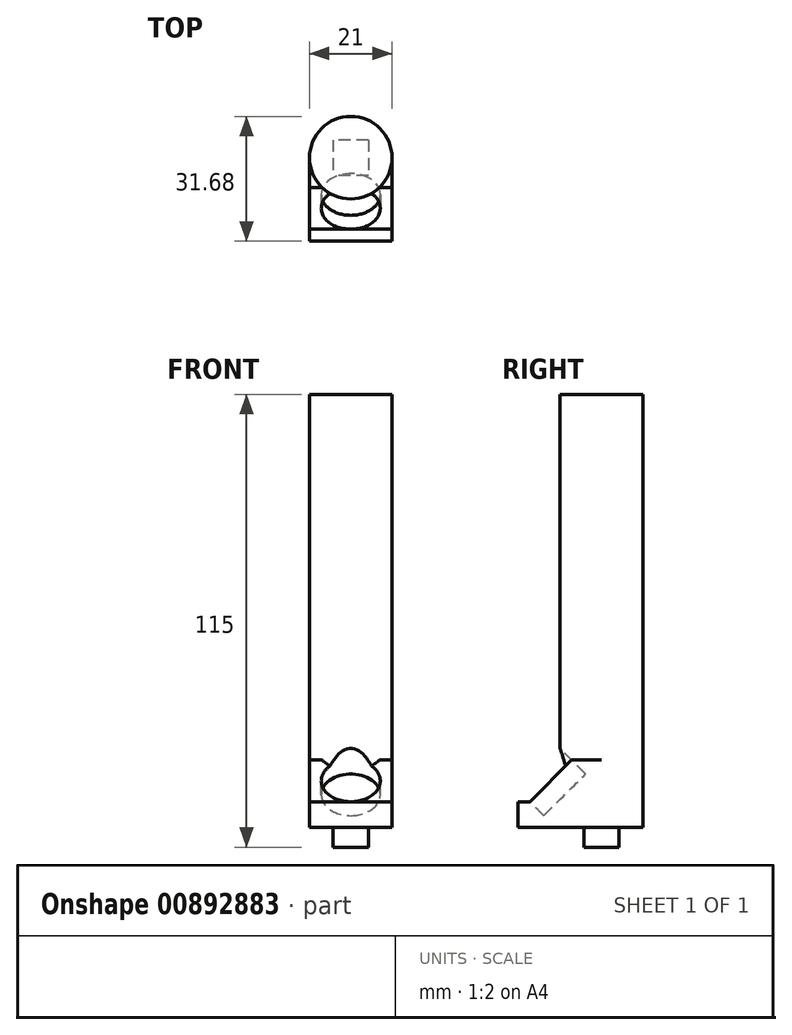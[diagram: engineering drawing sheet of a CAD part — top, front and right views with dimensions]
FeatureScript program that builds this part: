
annotation { "Feature Type Name" : "Feature", "Feature Type Description" : "" }
export const myFeature = defineFeature(function(context is Context, id is Id, definition is map)
    precondition{}
    {
        {
            var Q0;
            Q0=qCreatedBy(makeId("Top.planeOp"),FACE);
            var sketch = newSketch(context, id + "F0", { "sketchPlane" : qUnion([Q0])});
            skCircle(sketch, "E0", {"center": v(0, 0) * mm, "radius": 10.5 * mm});
            skSolve(sketch);
        }
        {
            var Q0;
            Q0=makeQuery(id+"F0.imprint","IMPRINT",FACE,{"disambiguationData":[TD([[makeQuery(id+"F0.imprint","IMPRINT",EDGE,{"derivedFrom":sQuery(id+"F0.wireOp",EDGE,"E0")}),1.0]])]});
            var Q1;
            Q1=sQuery(id+"F0.wireOp",EDGE,"E0");
            extrude(context, id + "F1", {"entities" : qUnion([Q0]), "surfaceEntities" : qUnion([Q1]), "depth" : 110 * mm, "offsetDistance" : 25 * mm});
        }
        {
            var Q0;
            Q0=qCreatedBy(makeId("Top.planeOp"),FACE);
            var sketch = newSketch(context, id + "F2", { "sketchPlane" : qUnion([Q0])});
            skLineSegment(sketch, "E1.bottom", {"start": v(4.5, 4.5) * mm, "end": v(-4.5, 4.5) * mm});
            skLineSegment(sketch, "E1.top", {"start": v(4.5, -4.5) * mm, "end": v(-4.5, -4.5) * mm});
            skLineSegment(sketch, "E1.left", {"start": v(4.5, 4.5) * mm, "end": v(4.5, -4.5) * mm});
            skLineSegment(sketch, "E1.right", {"start": v(-4.5, 4.5) * mm, "end": v(-4.5, -4.5) * mm});
            skPoint(sketch, "E1.middle", {"position": v(0, 0) * mm});
            skSolve(sketch);
        }
        {
            var Q0;
            Q0 = qSketchRegion(id + "F2", true);
            extrude(context, id + "F3", {"entities" : qUnion([Q0]), "operationType" : NewBodyOperationType.ADD, "oppositeDirection" : true, "depth" : 5 * mm, "offsetDistance" : 25 * mm});
        }
        {
            var Q0;
            Q0=qCreatedBy(makeId("Right.planeOp"),FACE);
            var sketch = newSketch(context, id + "F4", { "sketchPlane" : qUnion([Q0])});
            skLineSegment(sketch, "E2", {"start": v(0, 0) * mm, "end": v(-12.88, 0) * mm});
            skLineSegment(sketch, "E3", {"start": v(-12.88, 0) * mm, "end": v(-12.88, 11.84) * mm, "construction": true});
            skLineSegment(sketch, "E4", {"start": v(-12.88, 11.84) * mm, "end": v(-18.18, 11.84) * mm, "construction": true});
            skLineSegment(sketch, "E5", {"start": v(-18.18, 11.84) * mm, "end": v(-18.18, 6.54) * mm, "construction": true});
            skLineSegment(sketch, "E6", {"start": v(-18.18, 6.54) * mm, "end": v(-14.65, 6.54) * mm, "construction": true});
            skLineSegment(sketch, "E7", {"start": v(-14.65, 6.54) * mm, "end": v(-14.65, 3) * mm, "construction": true});
            skLineSegment(sketch, "E8", {"start": v(-12.88, 11.84) * mm, "end": v(-7.58, 11.84) * mm, "construction": true});
            skLineSegment(sketch, "E9", {"start": v(-7.58, 11.84) * mm, "end": v(-7.58, 17.14) * mm, "construction": true});
            skLineSegment(sketch, "E10", {"start": v(-7.58, 17.14) * mm, "end": v(-4.04, 17.14) * mm});
            skLineSegment(sketch, "E11", {"start": v(-4.04, 17.14) * mm, "end": v(-4.04, 13.6) * mm, "construction": true});
            skLineSegment(sketch, "E12", {"start": v(-7.58, 17.14) * mm, "end": v(-12.88, 11.84) * mm});
            skLineSegment(sketch, "E13", {"start": v(-12.88, 11.84) * mm, "end": v(-18.18, 6.54) * mm});
            skLineSegment(sketch, "E14", {"start": v(-18.18, 6.54) * mm, "end": v(-14.65, 3) * mm, "construction": true});
            skLineSegment(sketch, "E15", {"start": v(-14.65, 3) * mm, "end": v(-4.04, 13.6) * mm, "construction": true});
            skLineSegment(sketch, "E16", {"start": v(-4.04, 13.6) * mm, "end": v(-7.58, 17.14) * mm, "construction": true});
            skLineSegment(sketch, "E17", {"start": v(-18.18, 6.54) * mm, "end": v(-21.18, 6.54) * mm});
            skLineSegment(sketch, "E18", {"start": v(-21.18, 6.54) * mm, "end": v(-21.18, 0) * mm});
            skLineSegment(sketch, "E19", {"start": v(-4.04, 17.14) * mm, "end": v(0, 17.14) * mm});
            skLineSegment(sketch, "E20", {"start": v(0, 17.14) * mm, "end": v(0, 0) * mm});
            skLineSegment(sketch, "E21", {"start": v(-12.88, 0) * mm, "end": v(-21.18, 0) * mm});
            skSolve(sketch);
        }
        {
            var Q0;
            Q0=sQuery(id+"F4.wireOp",EDGE,"E12");
            var Q1;
            Q1=sQuery(id+"F4.wireOp",VERTEX,"E11.end");
            cPlane(context, id + "F5", {"entities" : qUnion([Q0, Q1]), "cplaneType" : CPlaneType.LINE_ANGLE, "offset" : 25 * mm, "angle" : 90 * degree, "width" : 150 * mm, "height" : 150 * mm});
        }
        {
            var Q0;
            Q0 = qSketchRegion(id + "F4", true);
            extrude(context, id + "F6", {"entities" : qUnion([Q0]), "operationType" : NewBodyOperationType.ADD, "depth" : 10.5 * mm, "offsetDistance" : 25 * mm, "hasSecondDirection" : true, "secondDirectionOppositeDirection" : true, "secondDirectionDepth" : 10.5 * mm});
        }
        {
            var Q0;
            Q0=qCreatedBy(id+"F5.planeOp",FACE);
            var sketch = newSketch(context, id + "F7", { "sketchPlane" : qUnion([Q0])});
            skPoint(sketch, "E22.0", {"position": v(0, -0.74) * mm});
            skCircle(sketch, "E23", {"center": v(0, -0.74) * mm, "radius": 7.5 * mm});
            skSolve(sketch);
        }
        {
            var Q0;
            Q0 = qSketchRegion(id + "F7", true);
            extrude(context, id + "F8", {"entities" : qUnion([Q0]), "operationType" : NewBodyOperationType.REMOVE, "oppositeDirection" : true, "depth" : 5 * mm, "offsetDistance" : 25 * mm, "hasSecondDirection" : true, "secondDirectionOppositeDirection" : false, "secondDirectionDepth" : 25 * mm});
        }
    });
